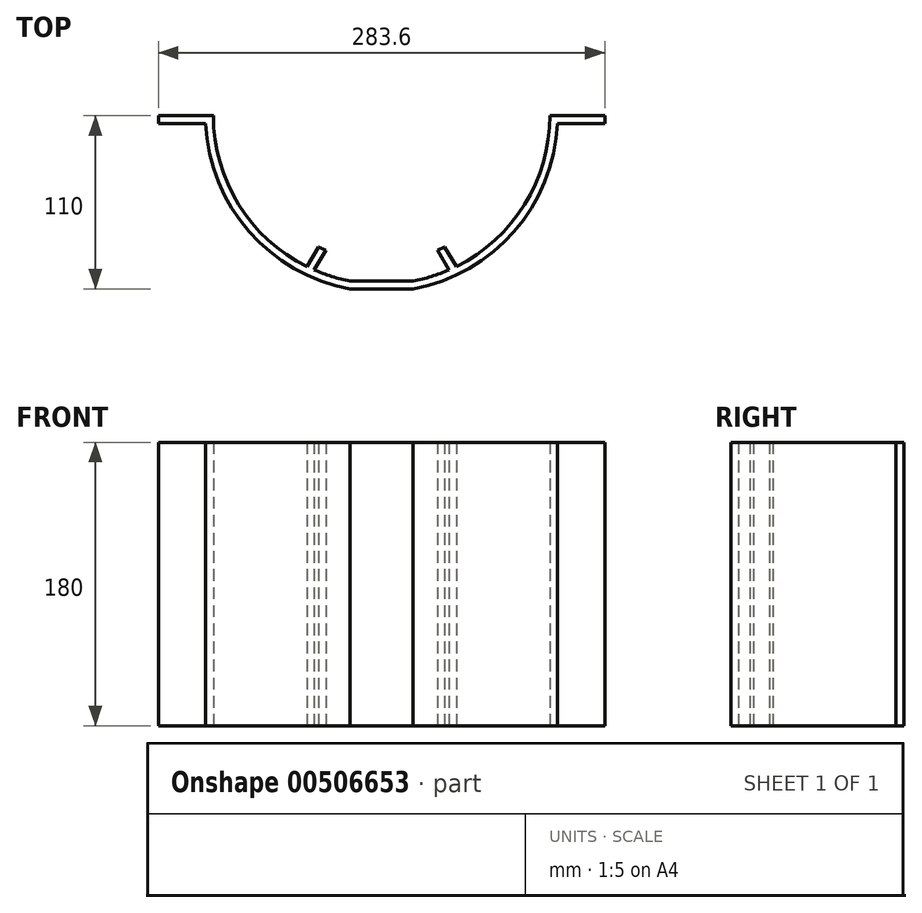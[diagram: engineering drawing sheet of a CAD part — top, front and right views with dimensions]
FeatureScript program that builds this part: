
annotation { "Feature Type Name" : "Feature", "Feature Type Description" : "" }
export const myFeature = defineFeature(function(context is Context, id is Id, definition is map)
    precondition{}
    {
        {
            var Q0;
            Q0=qCreatedBy(makeId("Top.planeOp"),FACE);
            var sketch = newSketch(context, id + "F0", { "sketchPlane" : qUnion([Q0])});
            skArc(sketch, "E0", {"start": v(35.4, -85.46) * mm, "mid": v(37.71, -84.46) * mm, "end": v(40, -83.4) * mm, "construction": true});
            skLineSegment(sketch, "E1", {"start": v(0, 0) * mm, "end": v(0, -132.62) * mm, "construction": true});
            skPoint(sketch, "E2.MirrorP", {"position": v(-37.87, -107.13) * mm});
            skPoint(sketch, "E3.MirrorP", {"position": v(-42.87, -110) * mm});
            skPoint(sketch, "E4.orphan", {"position": v(-119.37, -60) * mm});
            skLineSegment(sketch, "E5", {"start": v(20, -110) * mm, "end": v(-20, -110) * mm});
            skArc(sketch, "E6", {"start": v(20, -110) * mm, "mid": v(84.21, -73.54) * mm, "end": v(111.7, -5) * mm});
            skLineSegment(sketch, "E7", {"start": v(47.45, -95.78) * mm, "end": v(40, -83.4) * mm});
            skArc(sketch, "E8", {"start": v(35.4, -85.46) * mm, "mid": v(37.71, -84.46) * mm, "end": v(40, -83.4) * mm});
            skLineSegment(sketch, "E9.0", {"start": v(20, -105) * mm, "end": v(-20, -105) * mm});
            skArc(sketch, "E10", {"start": v(20, -105) * mm, "mid": v(31.65, -102.1) * mm, "end": v(42.9, -97.9) * mm});
            skLineSegment(sketch, "E11.trimOffspring", {"start": v(42.9, -97.9) * mm, "end": v(35.4, -85.46) * mm});
            skArc(sketch, "E12.trimOffspring", {"start": v(47.45, -95.78) * mm, "mid": v(90.82, -56.36) * mm, "end": v(106.89, 0) * mm});
            skPoint(sketch, "E13.orphan", {"position": v(50, -100) * mm});
            skLineSegment(sketch, "E14", {"start": v(111.8, 0) * mm, "end": v(106.89, 0) * mm});
            skLineSegment(sketch, "E15", {"start": v(111.8, 0) * mm, "end": v(141.8, 0) * mm});
            skLineSegment(sketch, "E16", {"start": v(141.8, 0) * mm, "end": v(141.8, -5) * mm});
            skLineSegment(sketch, "E17", {"start": v(141.8, -5) * mm, "end": v(111.7, -5) * mm});
            skLineSegment(sketch, "E18", {"start": v(-111.8, 0) * mm, "end": v(-141.8, 0) * mm});
            skLineSegment(sketch, "E19", {"start": v(-141.8, 0) * mm, "end": v(-141.8, -5) * mm});
            skLineSegment(sketch, "E20", {"start": v(-141.8, -5) * mm, "end": v(-111.7, -5) * mm});
            skLineSegment(sketch, "E21.trimOffspring", {"start": v(-106.89, 0) * mm, "end": v(-111.8, 0) * mm});
            skArc(sketch, "E22.trimOffspring", {"start": v(-111.7, -5) * mm, "mid": v(-84.21, -73.54) * mm, "end": v(-20, -110) * mm});
            skArc(sketch, "E23.trimOffspring", {"start": v(-106.89, 0) * mm, "mid": v(-90.82, -56.36) * mm, "end": v(-47.45, -95.78) * mm});
            skArc(sketch, "E24.MirrorCS", {"start": v(-35.4, -85.46) * mm, "mid": v(-37.71, -84.46) * mm, "end": v(-40, -83.4) * mm});
            skLineSegment(sketch, "E25.MirrorCS", {"start": v(-42.9, -97.9) * mm, "end": v(-35.4, -85.46) * mm});
            skLineSegment(sketch, "E26.MirrorCS", {"start": v(-47.45, -95.78) * mm, "end": v(-40, -83.4) * mm});
            skArc(sketch, "E27.MirrorCS", {"start": v(-35.4, -85.46) * mm, "mid": v(-37.71, -84.46) * mm, "end": v(-40, -83.4) * mm, "construction": true});
            skPoint(sketch, "E28.MirrorP", {"position": v(-50, -100) * mm});
            skArc(sketch, "E29.trimOffspring", {"start": v(-42.9, -97.9) * mm, "mid": v(-31.65, -102.1) * mm, "end": v(-20, -105) * mm});
            skSolve(sketch);
        }
        {
            var Q0;
            Q0 = qSketchRegion(id + "F0", true);
            extrude(context, id + "F1", {"entities" : qUnion([Q0]), "depth" : 180 * mm, "offsetDistance" : 25 * mm, "symmetric" : true});
        }
    });
